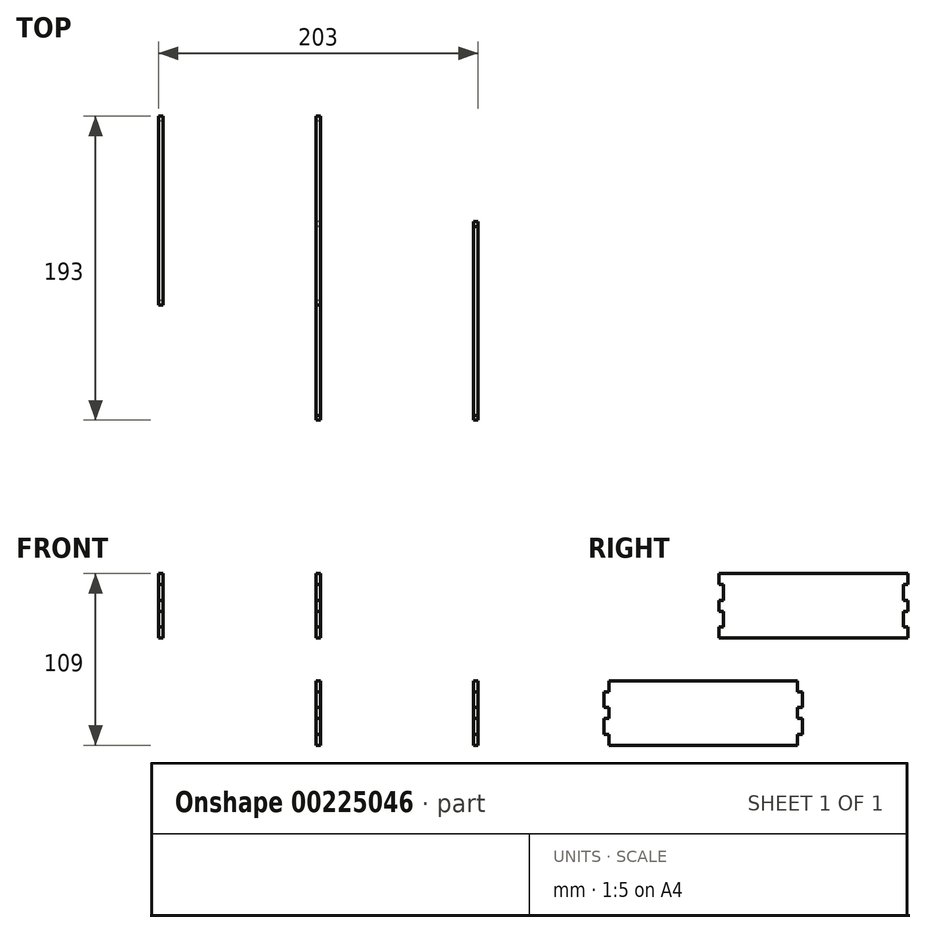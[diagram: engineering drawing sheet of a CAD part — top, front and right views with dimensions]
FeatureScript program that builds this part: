
annotation { "Feature Type Name" : "Feature", "Feature Type Description" : "" }
export const myFeature = defineFeature(function(context is Context, id is Id, definition is map)
    precondition{}
    {
        {
            var Q0;
            Q0=qCreatedBy(makeId("Right.planeOp"),FACE);
            var sketch = newSketch(context, id + "F0", { "sketchPlane" : qUnion([Q0])});
            skLineSegment(sketch, "E0", {"start": v(0, 0) * mm, "end": v(0, 7) * mm});
            skLineSegment(sketch, "E1", {"start": v(0, 7) * mm, "end": v(3, 7) * mm});
            skLineSegment(sketch, "E2", {"start": v(3, 7) * mm, "end": v(3, 17) * mm});
            skLineSegment(sketch, "E3", {"start": v(3, 17) * mm, "end": v(0, 17) * mm});
            skLineSegment(sketch, "E4", {"start": v(0, 17) * mm, "end": v(0, 24) * mm});
            skLineSegment(sketch, "E5", {"start": v(0, 24) * mm, "end": v(3, 24) * mm});
            skLineSegment(sketch, "E6", {"start": v(3, 24) * mm, "end": v(3, 34) * mm});
            skLineSegment(sketch, "E7", {"start": v(3, 34) * mm, "end": v(0, 34) * mm});
            skLineSegment(sketch, "E8", {"start": v(0, 34) * mm, "end": v(0, 41) * mm});
            skLineSegment(sketch, "E9.MirrorCS", {"start": v(-70, -61) * mm, "end": v(-73, -61) * mm});
            skLineSegment(sketch, "E10.MirrorCS", {"start": v(-70, -44) * mm, "end": v(-73, -44) * mm});
            skLineSegment(sketch, "E11.MirrorCS", {"start": v(-73, -34) * mm, "end": v(-70, -34) * mm});
            skLineSegment(sketch, "E12.MirrorCS", {"start": v(-73, -51) * mm, "end": v(-70, -51) * mm});
            skLineSegment(sketch, "E13.MirrorCS", {"start": v(-73, -61) * mm, "end": v(-73, -51) * mm});
            skLineSegment(sketch, "E14.MirrorCS", {"start": v(-70, -68) * mm, "end": v(-70, -61) * mm});
            skLineSegment(sketch, "E15.MirrorCS", {"start": v(-70, -34) * mm, "end": v(-70, -27) * mm});
            skLineSegment(sketch, "E16.MirrorCS", {"start": v(-73, -44) * mm, "end": v(-73, -34) * mm});
            skLineSegment(sketch, "E17.MirrorCS", {"start": v(-70, -51) * mm, "end": v(-70, -44) * mm});
            skLineSegment(sketch, "E18.MirrorCS", {"start": v(120, 34) * mm, "end": v(120, 41) * mm});
            skLineSegment(sketch, "E19.MirrorCS", {"start": v(117, 17) * mm, "end": v(120, 17) * mm});
            skLineSegment(sketch, "E20.MirrorCS", {"start": v(120, 24) * mm, "end": v(117, 24) * mm});
            skLineSegment(sketch, "E21.MirrorCS", {"start": v(117, 34) * mm, "end": v(120, 34) * mm});
            skLineSegment(sketch, "E22.MirrorCS", {"start": v(120, 17) * mm, "end": v(120, 24) * mm});
            skLineSegment(sketch, "E23.MirrorCS", {"start": v(120, 7) * mm, "end": v(117, 7) * mm});
            skLineSegment(sketch, "E24.MirrorCS", {"start": v(117, 7) * mm, "end": v(117, 17) * mm});
            skLineSegment(sketch, "E25.MirrorCS", {"start": v(117, 24) * mm, "end": v(117, 34) * mm});
            skLineSegment(sketch, "E26.MirrorCS", {"start": v(120, 0) * mm, "end": v(120, 7) * mm});
            skLineSegment(sketch, "E27", {"start": v(0, 41) * mm, "end": v(120, 41) * mm});
            skLineSegment(sketch, "E28", {"start": v(0, 0) * mm, "end": v(120, 0) * mm});
            skLineSegment(sketch, "E29.MirrorCS", {"start": v(50, -51) * mm, "end": v(50, -44) * mm});
            skLineSegment(sketch, "E30.MirrorCS", {"start": v(53, -34) * mm, "end": v(50, -34) * mm});
            skLineSegment(sketch, "E31.MirrorCS", {"start": v(53, -51) * mm, "end": v(50, -51) * mm});
            skLineSegment(sketch, "E32.MirrorCS", {"start": v(50, -61) * mm, "end": v(53, -61) * mm});
            skLineSegment(sketch, "E33.MirrorCS", {"start": v(50, -44) * mm, "end": v(53, -44) * mm});
            skLineSegment(sketch, "E34.MirrorCS", {"start": v(50, -34) * mm, "end": v(50, -27) * mm});
            skLineSegment(sketch, "E35.MirrorCS", {"start": v(50, -68) * mm, "end": v(50, -61) * mm});
            skLineSegment(sketch, "E36.MirrorCS", {"start": v(53, -61) * mm, "end": v(53, -51) * mm});
            skLineSegment(sketch, "E37.MirrorCS", {"start": v(53, -44) * mm, "end": v(53, -34) * mm});
            skLineSegment(sketch, "E38", {"start": v(-70, -27) * mm, "end": v(50, -27) * mm});
            skLineSegment(sketch, "E39", {"start": v(-70, -68) * mm, "end": v(50, -68) * mm});
            skPoint(sketch, "E40.end.orphan", {"position": v(60, 0) * mm});
            skSolve(sketch);
        }
        {
            var Q0;
            Q0=qSketchRegion(id+"F0",true);
            extrude(context, id + "F1", {"entities" : qUnion([Q0]), "endBound" : BoundingType.SYMMETRIC, "depth" : 3 * mm});
        }
        {
            var Q0;
            Q0=makeQuery(id+"F1.opExtrude","SWEPT_BODY",BODY,{"disambiguationData":[OSD([sQuery(id+"F0.wireOp",EDGE,"E12.MirrorCS"),sQuery(id+"F0.wireOp",EDGE,"E11.MirrorCS"),sQuery(id+"F0.wireOp",EDGE,"E10.MirrorCS"),sQuery(id+"F0.wireOp",EDGE,"E9.MirrorCS"),sQuery(id+"F0.wireOp",EDGE,"E13.MirrorCS"),sQuery(id+"F0.wireOp",EDGE,"E15.MirrorCS"),sQuery(id+"F0.wireOp",EDGE,"E17.MirrorCS"),sQuery(id+"F0.wireOp",EDGE,"E14.MirrorCS"),sQuery(id+"F0.wireOp",EDGE,"E16.MirrorCS"),sQuery(id+"F0.wireOp",EDGE,"E29.MirrorCS"),sQuery(id+"F0.wireOp",EDGE,"E32.MirrorCS"),sQuery(id+"F0.wireOp",EDGE,"E31.MirrorCS"),sQuery(id+"F0.wireOp",EDGE,"E30.MirrorCS"),sQuery(id+"F0.wireOp",EDGE,"E33.MirrorCS"),sQuery(id+"F0.wireOp",EDGE,"E35.MirrorCS"),sQuery(id+"F0.wireOp",EDGE,"E34.MirrorCS"),sQuery(id+"F0.wireOp",EDGE,"E36.MirrorCS"),sQuery(id+"F0.wireOp",EDGE,"E37.MirrorCS"),sQuery(id+"F0.wireOp",EDGE,"E38"),sQuery(id+"F0.wireOp",EDGE,"E39")])]});
            transform(context, id + "F2", {"entities" : qUnion([Q0]), "transformType" : TransformType.TRANSLATION_3D, "dx" : 100 * mm, "dy" : 0 * mm, "dz" : 0 * mm, "makeCopy" : true});
        }
        {
            var Q0;
            Q0=makeQuery(id+"F1.opExtrude","SWEPT_BODY",BODY,{"disambiguationData":[OSD([sQuery(id+"F0.wireOp",EDGE,"E0"),sQuery(id+"F0.wireOp",EDGE,"E1"),sQuery(id+"F0.wireOp",EDGE,"E2"),sQuery(id+"F0.wireOp",EDGE,"E3"),sQuery(id+"F0.wireOp",EDGE,"E4"),sQuery(id+"F0.wireOp",EDGE,"E5"),sQuery(id+"F0.wireOp",EDGE,"E6"),sQuery(id+"F0.wireOp",EDGE,"E7"),sQuery(id+"F0.wireOp",EDGE,"E8"),sQuery(id+"F0.wireOp",EDGE,"E18.MirrorCS"),sQuery(id+"F0.wireOp",EDGE,"E19.MirrorCS"),sQuery(id+"F0.wireOp",EDGE,"E20.MirrorCS"),sQuery(id+"F0.wireOp",EDGE,"E21.MirrorCS"),sQuery(id+"F0.wireOp",EDGE,"E22.MirrorCS"),sQuery(id+"F0.wireOp",EDGE,"E23.MirrorCS"),sQuery(id+"F0.wireOp",EDGE,"E24.MirrorCS"),sQuery(id+"F0.wireOp",EDGE,"E25.MirrorCS"),sQuery(id+"F0.wireOp",EDGE,"E26.MirrorCS"),sQuery(id+"F0.wireOp",EDGE,"E27"),sQuery(id+"F0.wireOp",EDGE,"E28")])]});
            transform(context, id + "F3", {"entities" : qUnion([Q0]), "transformType" : TransformType.TRANSLATION_3D, "dx" : -100 * mm, "dy" : 0 * mm, "dz" : 0 * mm, "makeCopy" : true});
        }
    });
